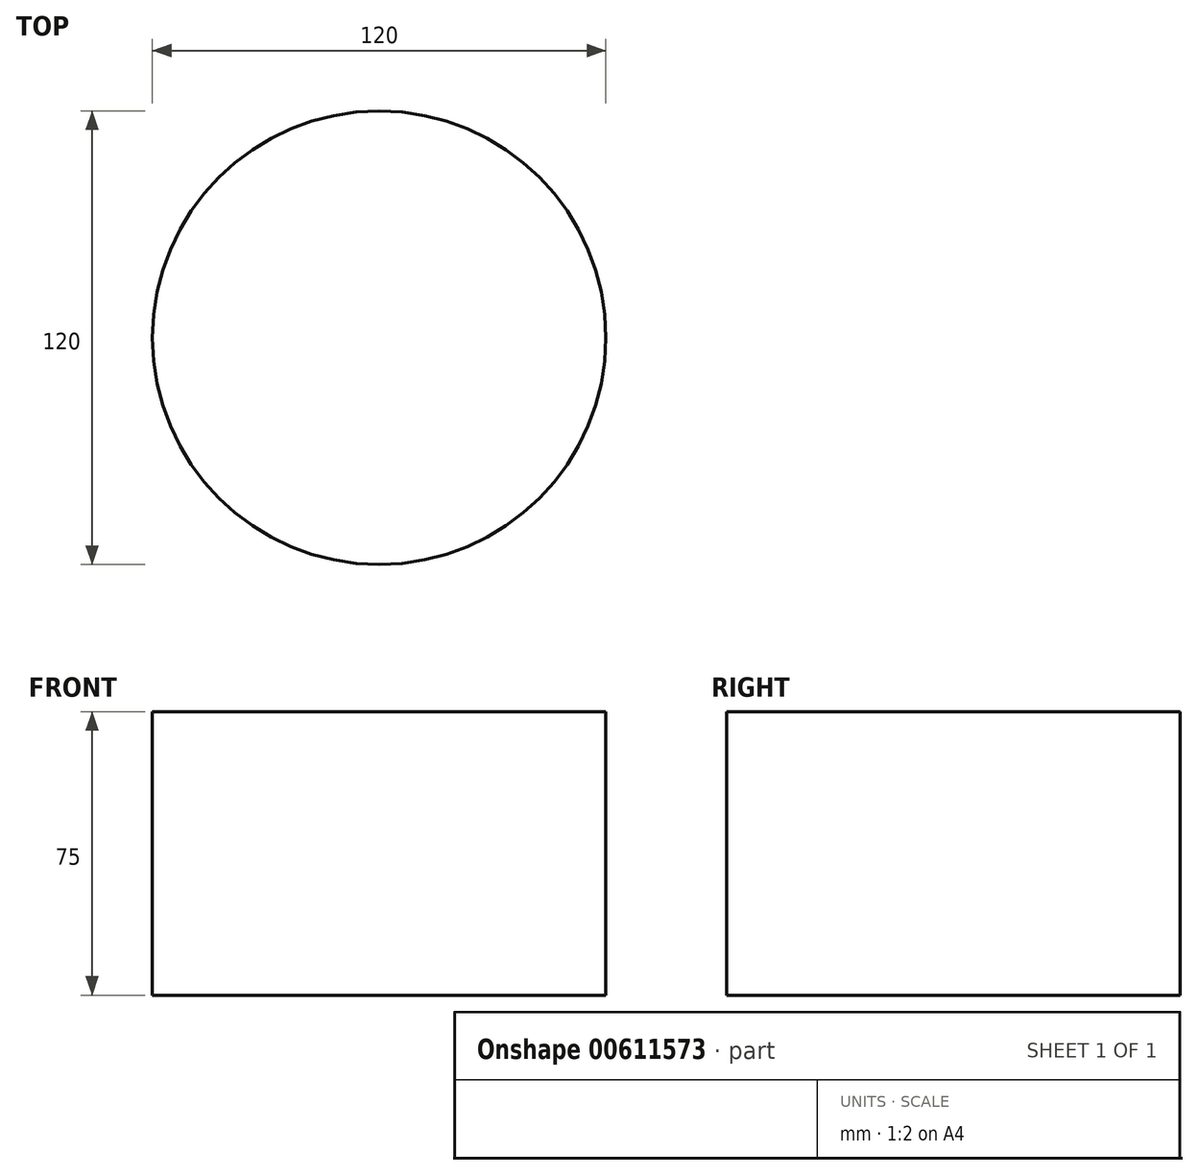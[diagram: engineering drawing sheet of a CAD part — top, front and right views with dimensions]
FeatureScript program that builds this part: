
annotation { "Feature Type Name" : "Feature", "Feature Type Description" : "" }
export const myFeature = defineFeature(function(context is Context, id is Id, definition is map)
    precondition{}
    {
        {
            var Q0;
            Q0=qCreatedBy(makeId("Top.planeOp"),FACE);
            var sketch = newSketch(context, id + "F0", { "sketchPlane" : qUnion([Q0])});
            skCircle(sketch, "E0", {"center": v(0, 0) * mm, "radius": 60 * mm});
            skSolve(sketch);
        }
        {
            var Q0;
            Q0 = qSketchRegion(id + "F0", true);
            var Q1;
            Q1=sQuery(id+"F0.wireOp",EDGE,"E0");
            extrude(context, id + "F1", {"entities" : qUnion([Q0]), "bodyType" : ToolBodyType.SURFACE, "surfaceEntities" : qUnion([Q1]), "depth" : 75 * mm, "offsetDistance" : 25 * mm});
        }
    });
